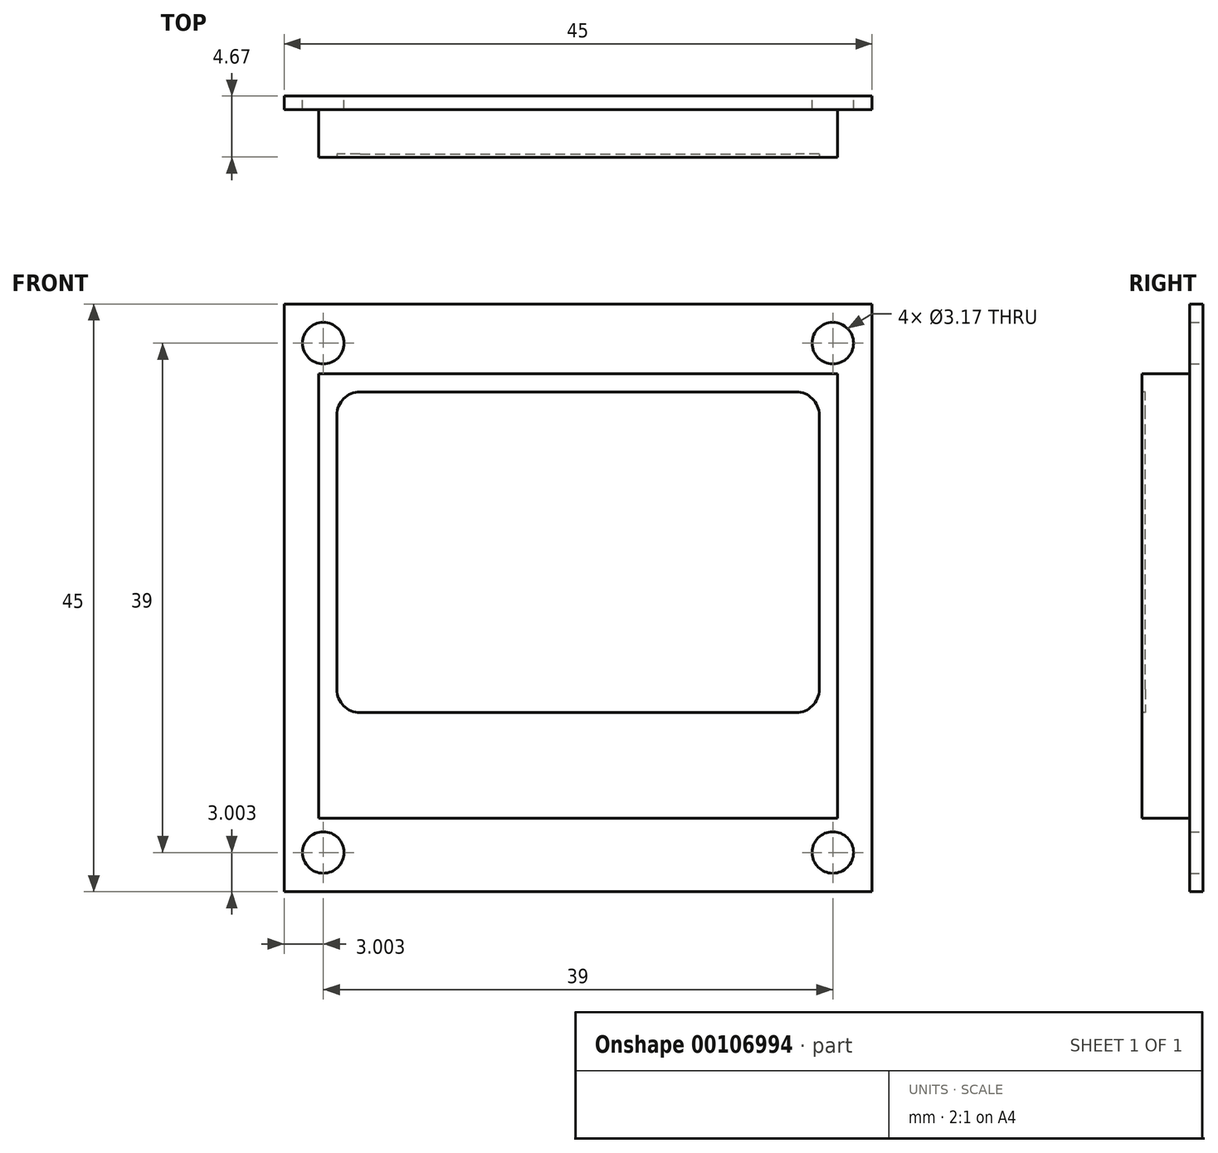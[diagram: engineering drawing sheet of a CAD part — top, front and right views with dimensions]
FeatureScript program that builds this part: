
annotation { "Feature Type Name" : "Feature", "Feature Type Description" : "" }
export const myFeature = defineFeature(function(context is Context, id is Id, definition is map)
    precondition{}
    {
        {
            var Q0;
            Q0=qCreatedBy(makeId("Front.planeOp"),FACE);
            var sketch = newSketch(context, id + "F0", { "sketchPlane" : qUnion([Q0])});
            skLineSegment(sketch, "E0.bottom", {"start": v(-72.76, 54.07) * mm, "end": v(-117.76, 54.07) * mm});
            skLineSegment(sketch, "E0.top", {"start": v(-72.76, 9.07) * mm, "end": v(-117.76, 9.07) * mm});
            skLineSegment(sketch, "E0.left", {"start": v(-72.76, 54.07) * mm, "end": v(-72.76, 9.07) * mm});
            skLineSegment(sketch, "E0.right", {"start": v(-117.76, 54.07) * mm, "end": v(-117.76, 9.07) * mm});
            skPoint(sketch, "E0.middle", {"position": v(-95.26, 31.57) * mm});
            skLineSegment(sketch, "E1.0", {"start": v(-75.76, 51.07) * mm, "end": v(-114.76, 51.07) * mm});
            skLineSegment(sketch, "E1.1", {"start": v(-75.76, 51.07) * mm, "end": v(-75.76, 48.74) * mm});
            skLineSegment(sketch, "E1.2", {"start": v(-75.76, 12.07) * mm, "end": v(-114.76, 12.07) * mm});
            skLineSegment(sketch, "E1.3", {"start": v(-114.76, 51.07) * mm, "end": v(-114.76, 48.74) * mm});
            skCircle(sketch, "E2", {"center": v(-75.76, 51.07) * mm, "radius": 1.59 * mm});
            skCircle(sketch, "E3", {"center": v(-114.76, 51.07) * mm, "radius": 1.59 * mm});
            skCircle(sketch, "E4", {"center": v(-114.76, 12.07) * mm, "radius": 1.59 * mm});
            skCircle(sketch, "E5", {"center": v(-75.76, 12.07) * mm, "radius": 1.59 * mm});
            skLineSegment(sketch, "E6.bottom", {"start": v(-115.12, 14.7) * mm, "end": v(-75.4, 14.7) * mm});
            skLineSegment(sketch, "E6.top", {"start": v(-115.12, 48.74) * mm, "end": v(-75.4, 48.74) * mm});
            skLineSegment(sketch, "E6.left", {"start": v(-115.12, 14.7) * mm, "end": v(-115.12, 48.74) * mm});
            skLineSegment(sketch, "E6.right", {"start": v(-75.4, 14.7) * mm, "end": v(-75.4, 48.74) * mm});
            skLineSegment(sketch, "E7.trimOffspring", {"start": v(-114.76, 14.7) * mm, "end": v(-114.76, 12.07) * mm});
            skLineSegment(sketch, "E8.trimOffspring", {"start": v(-75.76, 14.7) * mm, "end": v(-75.76, 12.07) * mm});
            skSolve(sketch);
        }
        {
            var Q0;
            Q0 = qSketchRegion(id + "F0", true);
            var Q1;
            {var subQ0=sQuery(id+"F0.wireOp",EDGE,"E2");var subQ1=sQuery(id+"F0.wireOp",EDGE,"E1.0");var subQ2=makeQuery(id+"F0.imprint","INTERSECT",VERTEX,{"derivedFrom":[subQ1,subQ0]});Q1=makeQuery(id+"F0.imprint","IMPRINT",FACE,{"disambiguationData":[TD([[makeQuery(id+"F0.imprint","IMPRINT",EDGE,{"disambiguationData":[TD([[subQ2,-1.0]])],"derivedFrom":subQ1}),1.0]])]});}
            var Q2;
            {var subQ0=sQuery(id+"F0.wireOp",EDGE,"E5");var subQ1=sQuery(id+"F0.wireOp",EDGE,"E1.2");var subQ2=makeQuery(id+"F0.imprint","INTERSECT",VERTEX,{"derivedFrom":[subQ1,subQ0]});Q2=makeQuery(id+"F0.imprint","IMPRINT",FACE,{"disambiguationData":[TD([[makeQuery(id+"F0.imprint","IMPRINT",EDGE,{"disambiguationData":[TD([[subQ2,-1.0]])],"derivedFrom":subQ1}),-1.0]])]});}
            extrude(context, id + "F1", {"entities" : qUnion([Q0, Q1, Q2]), "depth" : 1.04 * mm});
        }
        {
            var Q0;
            {var subQ2=sQuery(id+"F0.wireOp",EDGE,"E6.left");Q0=makeQuery(id+"F0.imprint","IMPRINT",FACE,{"disambiguationData":[TD([[makeQuery(id+"F0.imprint","IMPRINT",EDGE,{"derivedFrom":subQ2}),-1.0]])]});}
            extrude(context, id + "F2", {"entities" : qUnion([Q0]), "operationType" : NewBodyOperationType.ADD, "depth" : 4.67 * mm});
        }
        {
            var Q0;
            Q0=makeQuery(id+"F2.opExtrude","CAP_FACE",FACE,{"disambiguationData":[OSD([sQuery(id+"F0.wireOp",EDGE,"E6.bottom"),sQuery(id+"F0.wireOp",EDGE,"E6.top"),sQuery(id+"F0.wireOp",EDGE,"E6.left"),sQuery(id+"F0.wireOp",EDGE,"E6.right")])],"isStart":false});
            var sketch = newSketch(context, id + "F3", { "sketchPlane" : qUnion([Q0])});
            skLineSegment(sketch, "E9.0", {"start": v(-111.94, 47.34) * mm, "end": v(-78.57, 47.34) * mm});
            skLineSegment(sketch, "E9.1", {"start": v(-113.72, 24.56) * mm, "end": v(-113.72, 45.56) * mm});
            skLineSegment(sketch, "E9.2", {"start": v(-113.72, 16.1) * mm, "end": v(-76.8, 16.1) * mm});
            skLineSegment(sketch, "E9.3", {"start": v(-76.8, 24.56) * mm, "end": v(-76.8, 45.56) * mm});
            skLineSegment(sketch, "E10", {"start": v(-111.94, 22.78) * mm, "end": v(-78.57, 22.78) * mm});
            skPoint(sketch, "E11.visualSharp", {"position": v(-113.72, 47.34) * mm});
            skArc(sketch, "E11.filletArc", {"start": v(-111.94, 47.34) * mm, "mid": v(-113.2, 46.82) * mm, "end": v(-113.72, 45.56) * mm});
            skPoint(sketch, "E12.visualSharp", {"position": v(-76.8, 47.34) * mm});
            skArc(sketch, "E12.filletArc", {"start": v(-76.8, 45.56) * mm, "mid": v(-77.32, 46.82) * mm, "end": v(-78.57, 47.34) * mm});
            skArc(sketch, "E13.filletArc", {"start": v(-78.57, 22.78) * mm, "mid": v(-77.32, 23.3) * mm, "end": v(-76.8, 24.56) * mm});
            skArc(sketch, "E14.filletArc", {"start": v(-113.72, 24.56) * mm, "mid": v(-113.2, 23.3) * mm, "end": v(-111.94, 22.78) * mm});
            skSolve(sketch);
        }
        {
            var Q0;
            Q0=makeQuery(id+"F3.imprint","IMPRINT",FACE,{"disambiguationData":[TD([[makeQuery(id+"F3.imprint","IMPRINT",EDGE,{"derivedFrom":sQuery(id+"F3.wireOp",EDGE,"E9.0")}),-1.0]])]});
            extrude(context, id + "F4", {"entities" : qUnion([Q0]), "operationType" : NewBodyOperationType.REMOVE, "oppositeDirection" : true, "depth" : 0.25 * mm});
        }
    });
